# Revit family: boiler_eutectic-cast-iron_gt-530a_ea_ddr-americas_RVT2016
name_source: partatom
category: Equipement de génie climatique
revit_build: Autodesk Revit 2016 (Build: 20161004_0715(x64)
units: mm (PartAtom-declared; Revit-internal decimal feet)

## family parameters
Basée sur le plan de construction = Non
Cote de connecteur circulaire = Utiliser le diamètre
Couper avec des vides une fois chargée = Non
Numéro OmniClass = 23.75.10.11.14.11
Partagée = Non
Point de calcul de pièce = Non
Titre OmniClass = Cast-Iron Boilers
Toujours verticalement = Oui
Type d'élément = Normal

## types (18) — shared parameters
0 Message = User to Refer to De Dietrich Technical Data Sheet
04 CSI = 23 52 23
95 CSI = 15510
ASME Rating MAWP = 90
Approvals = CSA, MASS, NY-DEP, ASME, CSD-1, Low Nox certified, CRN
BMS Protocol = BACnet
Category = Mechanical Equipment
Code d'assemblage = D3020100
Description = Near-Condensing Eutectic Cast Iron Boiler
Efficiency = 88.00%
Fabricant = De Dietrich Boilers / DDR Americas Inc.
Firing Turndown Ratio = 5:1
Frequency = 60 Hz
Gas Pressure = 7-14 Inches w.c.
Gas-vent Category = I, II, III, IV, Sidewall vented and Direct vent (sealed combustion air)
Heat Exchanger Material = Cast Iron
Installation/Operating Instructions = http://www.dedietrichboilers.com
Low Nox - Optional = Oui
Manufacturer Fax = 519-650-1709
Max Water Temp Safety Limit = 248 °F
Nominal Width = 46 "
Phase = 1
Piping Layout = http://www.dedietrichboilers.com
Product Brochure = http://www.dedietrichboilers.com
Product Page URL = http://www.dedietrichboilers.com
SMARTBIM Object Version = 3
SMARTBIM URL = http://www.SMARTBIM.com
Specifications URL = http://www.dedietrichboilers.com
Subcategory = Gas-Oil Fired Eutectic Cast Iron Boiler
URL = http://www.dedietrichboilers.com
Voltage = 120 V
Water Operating Temp Range °F /°C = 104-212°F / 40-100°C
ØE = 5.5 "
zero-valued in all types: Gas Connection

## per-type parameters (varying)
- GT 530A-15: # Sections=15; #2 Fuel Oil Input=26 USGPH; A=98.18 "; B=34.14 "; Boiler-vent Connection=16 "; C=58.58 "; Dry Weight=7416.00 lb; Efficiency Natural Gas=85.00%; Full Load Amps=<15A; G=50 "; Gas Input=1099 kW; H=-1.22 "; Height=65.75 "; Installed Weight=8940.00 lb; K=0.75 "; L=88.39 "; M=7.4 "; Modèle=GT 530A-15; N=42.52 "; Nominal Height=65.75 "; Nominal Length=88.39 "; Output [Gas-Oil]=936.2 kW; P=32.09 "; Plates=Plastic Dark; R=7.87 "; Radius F=8 "; Unit=Paint Ivory Glossy; Water Capacity=183.1 gal; Water Resistance Delta T -18 F (Ft. H2O)=3.277; Water Resistance Delta T -27 F (Ft. H2O)=1.456; Water Resistance Delta T -36 F (Ft. H2O)=0.819; _C=58.58 "; _K=0.75 "; ØF=7.88 "
- GT 530A-16: # Sections=16; #2 Fuel Oil Input=27.5 USGPH; A=102.56 "; B=34.14 "; Boiler-vent Connection=16 "; C=58.58 "; Dry Weight=7851.00 lb; Efficiency Natural Gas=0.00%; Full Load Amps=<15A; G=5.9 "; Gas Input=1162 kW; H=-1.18 "; Height=65.75 "; Installed Weight=9460.00 lb; K=0.71 "; L=92.72 "; M=7.44 "; Modèle=GT 530A-16; N=42.52 "; Nominal Height=65.75 "; Nominal Length=92.72 "; Output [Gas-Oil]=990.2 kW; P=32.09 "; Plates=Aluminum Anodized; R=7.87 "; Radius F=8 "; Unit=Aluminum Polished; Water Capacity=193.2 gal; Water Resistance Delta T -18 F (Ft. H2O)=1.085; Water Resistance Delta T -27 F (Ft. H2O)=0.483; Water Resistance Delta T -36 F (Ft. H2O)=0.271; _C=58.58 "; _K=0.71 "; ØF=7.88 "
- GT 530A-17: # Sections=17; #2 Fuel Oil Input=29.5 USGPH; A=106.93 "; B=34.14 "; Boiler-vent Connection=16 "; C=58.58 "; Dry Weight=8280.00 lb; Efficiency Natural Gas=85.00%; Full Load Amps=<15A; G=14.57 "; Gas Input=1247 kW; H=-0.35 "; Height=65.75 "; Installed Weight=9970.00 lb; K=0.12 "; L=96.26 "; M=8.26 "; Modèle=GT 530A-17; N=42.52 "; Nominal Height=65.75 "; Nominal Length=96.26 "; Output [Gas-Oil]=1062.2 kW; P=32.09 "; Plates=Aluminum Anodized; R=7.87 "; Radius F=8 "; Unit=Aluminum Polished; Water Capacity=203.2 gal; Water Resistance Delta T -18 F (Ft. H2O)=1.279; Water Resistance Delta T -27 F (Ft. H2O)=0.569; Water Resistance Delta T -36 F (Ft. H2O)=0.32; _C=58.58 "; _K=0.12 "; ØF=7.88 "
- GT 530A-18: # Sections=18; #2 Fuel Oil Input=31 USGPH; A=112.68 "; B=34.14 "; Boiler-vent Connection=16 "; C=59.2 "; Dry Weight=8719.00 lb; Efficiency Natural Gas=0.00%; Full Load Amps=<15A; G=14.57 "; Gas Input=1310 kW; H=-0.32 "; Height=65.75 "; Installed Weight=10495.00 lb; K=0.16 "; L=100.59 "; M=9.29 "; Modèle=GT 530A-18; N=45.52 "; Nominal Height=65.75 "; Nominal Length=100.59 "; Output [Gas-Oil]=1188.3 kW; P=32.09 "; Plates=Aluminum Anodized; R=7.87 "; Radius F=8 "; Unit=Aluminum Polished; Water Capacity=213.2 gal; Water Resistance Delta T -18 F (Ft. H2O)=1.446; Water Resistance Delta T -27 F (Ft. H2O)=0.643; Water Resistance Delta T -36 F (Ft. H2O)=0.361; _C=59.2 "; _K=0.16 "; ØF=7.88 "
- GT 530A-19: # Sections=19; #2 Fuel Oil Input=33 USGPH; A=117.05 "; B=34.14 "; Boiler-vent Connection=16 "; C=59.2 "; Dry Weight=9092.00 lb; Efficiency Natural Gas=0.00%; Full Load Amps=<15A; G=14.57 "; Gas Input=1395 kW; H=0.51 "; Height=65.75 "; Installed Weight=10950.00 lb; K=0.98 "; L=104.13 "; M=10.12 "; Modèle=GT 530A-19; N=42.52 "; Nominal Height=65.75 "; Nominal Length=104.13 "; Output [Gas-Oil]=1188.3 kW; P=32.09 "; Plates=Aluminum Anodized; R=7.87 "; Radius F=8 "; Unit=Aluminum Polished; Water Capacity=223.3 gal; Water Resistance Delta T -18 F (Ft. H2O)=1.753; Water Resistance Delta T -27 F (Ft. H2O)=0.779; Water Resistance Delta T -36 F (Ft. H2O)=0.438; _C=59.2 "; _K=0.98 "; ØF=7.88 "
- GT 530A-20: # Sections=20; #2 Fuel Oil Input=34.5 USGPH; A=122.99 "; B=34.14 "; Boiler-vent Connection=16 "; C=59.2 "; Dry Weight=9575.00 lb; Efficiency Natural Gas=0.00%; Full Load Amps=<15A; G=25.59 "; Gas Input=1458 kW; H=-1.42 "; Height=65.75 "; Installed Weight=11565.00 lb; K=0.95 "; L=112.01 "; M=8.19 "; Modèle=GT 530A-20; N=42.52 "; Nominal Height=65.75 "; Nominal Length=112.01 "; Output [Gas-Oil]=1242.3 kW; P=32.09 "; Plates=Aluminum Anodized; R=7.87 "; Radius F=8 "; Unit=Aluminum Polished; Water Capacity=239.1 gal; Water Resistance Delta T -18 F (Ft. H2O)=1.999; Water Resistance Delta T -27 F (Ft. H2O)=0.889; Water Resistance Delta T -36 F (Ft. H2O)=0.5; _C=59.2 "; _K=0.95 "; ØF=7.88 "
- GT 530A-21: # Sections=21; #2 Fuel Oil Input=36 USGPH; A=127.36 "; B=34.14 "; Boiler-vent Connection=16 "; C=59.2 "; Dry Weight=10004.00 lb; Efficiency Natural Gas=0.00%; Full Load Amps=<15A; G=25.59 "; Gas Input=1521 kW; H=-1.38 "; Height=65.75 "; Installed Weight=12080.00 lb; K=0.91 "; L=116.34 "; M=8.22 "; Modèle=GT 530A-21; N=45.52 "; Nominal Height=65.75 "; Nominal Length=116.34 "; Output [Gas-Oil]=1296.3 kW; P=32.09 "; Plates=Aluminum Anodized; R=7.87 "; Radius F=9 "; Unit=Aluminum Polished; Water Capacity=249.1 gal; Water Resistance Delta T -18 F (Ft. H2O)=2.209; Water Resistance Delta T -27 F (Ft. H2O)=0.982; Water Resistance Delta T -36 F (Ft. H2O)=0.552; _C=59.2 "; _K=0.91 "; ØF=9 "
- GT 530A-22: # Sections=22; #2 Fuel Oil Input=38 USGPH; A=131.73 "; B=34.14 "; Boiler-vent Connection=18 "; C=59.2 "; Dry Weight=10437.00 lb; Efficiency Natural Gas=0.00%; Full Load Amps=<15A; G=25.59 "; Gas Input=1606 kW; H=-0.55 "; Height=65.75 "; Installed Weight=12595.00 lb; K=0.08 "; L=119.88 "; M=9.05 "; Modèle=GT 530A-22; N=42.52 "; Nominal Height=65.75 "; Nominal Length=119.88 "; Output [Gas-Oil]=1368.3 kW; P=32.09 "; Plates=Aluminum Anodized; R=7.87 "; Radius F=9 "; Unit=Aluminum Polished; Water Capacity=259.2 gal; Water Resistance Delta T -18 F (Ft. H2O)=2.476; Water Resistance Delta T -27 F (Ft. H2O)=1.101; Water Resistance Delta T -36 F (Ft. H2O)=0.619; _C=59.2 "; _K=0.08 "; ØF=9 "
- GT 530A-23: # Sections=23; #2 Fuel Oil Input=39.5 USGPH; A=131.73 "; B=34.14 "; Boiler-vent Connection=18 "; C=59.2 "; Dry Weight=10869.00 lb; Efficiency Natural Gas=0.00%; Full Load Amps=<15A; G=38.58 "; Gas Input=1669 kW; H=-0.51 "; Height=65.75 "; Installed Weight=13110.00 lb; K=0.04 "; L=124.21 "; M=9.05 "; Modèle=GT 530A-23; N=42.52 "; Nominal Height=65.75 "; Nominal Length=124.21 "; Output [Gas-Oil]=1422.3 kW; P=32.09 "; Plates=Aluminum Anodized; R=7.87 "; Radius F=9 "; Unit=Aluminum Polished; Water Capacity=269.2 gal; Water Resistance Delta T -18 F (Ft. H2O)=2.703; Water Resistance Delta T -27 F (Ft. H2O)=1.201; Water Resistance Delta T -36 F (Ft. H2O)=0.676; _C=59.2 "; _K=0.04 "; ØF=9 "
- GT 530A-24: # Sections=24; #2 Fuel Oil Input=41.5 USGPH; A=140.47 "; B=34.14 "; Boiler-vent Connection=18 "; C=59.2 "; Dry Weight=11259.00 lb; Efficiency Natural Gas=0.00%; Full Load Amps=<15A; G=38.58 "; Gas Input=1754 kW; H=0.32 "; Height=65.75 "; Installed Weight=13585.00 lb; K=0.79 "; L=127.76 "; M=9.92 "; Modèle=GT 530A-24; N=42.52 "; Nominal Height=65.75 "; Nominal Length=127.76 "; Output [Gas-Oil]=1494.3 kW; P=32.09 "; Plates=Aluminum Anodized; R=7.87 "; Radius F=9 "; Unit=Aluminum Polished; Water Capacity=279.3 gal; Water Resistance Delta T -18 F (Ft. H2O)=3.014; Water Resistance Delta T -27 F (Ft. H2O)=1.339; Water Resistance Delta T -36 F (Ft. H2O)=0.753; _C=59.2 "; _K=0.79 "; ØF=9 "
- GT 530A-25: # Sections=25; #2 Fuel Oil Input=43 USGPH; A=144.84 "; B=34.14 "; Boiler-vent Connection=18 "; C=59.2 "; Dry Weight=11678.00 lb; Efficiency Natural Gas=0.00%; Full Load Amps=<15A; G=38.58 "; Gas Input=1817 kW; H=0.35 "; Height=65.75 "; Installed Weight=14085.00 lb; K=0.83 "; L=132.09 "; M=9.96 "; Modèle=GT 530A-25; N=42.52 "; Nominal Height=65.75 "; Nominal Length=132.09 "; Output [Gas-Oil]=1548.3 kW; P=32.09 "; Plates=Aluminum Anodized; R=7.87 "; Radius F=9 "; Unit=Aluminum Polished; Water Capacity=289.4 gal; Water Resistance Delta T -18 F (Ft. H2O)=3.269; Water Resistance Delta T -27 F (Ft. H2O)=1.452; Water Resistance Delta T -36 F (Ft. H2O)=0.817; _C=59.2 "; _K=0.83 "; ØF=9 "
- GT 530AE-26: # Sections=26; #2 Fuel Oil Input=43.8 USGPH; A=154.37 "; B=37.14 "; Boiler-vent Connection=20 "; C=65 "; Dry Weight=12111.00 lb; Efficiency Natural Gas=0.00%; Full Load Amps=<15A fused; G=41.6 "; Gas Input=1900 kW; H=1.02 "; Height=68.75 "; Installed Weight=0.00 lb; K=1.81 "; L=138.8 "; M=19.53 "; Modèle=GT 530A-26; N=45.52 "; Nominal Height=68.75 "; Nominal Length=138.8 "; Output [Gas-Oil]=1618.8 kW; P=35.09 "; Plates=Aluminum Anodized; R=10.87 "; Radius F=10 "; Unit=Aluminum Polished; Water Capacity=299.4 gal; Water Resistance Delta T -18 F (Ft. H2O)=3.48; Water Resistance Delta T -27 F (Ft. H2O)=1.55; Water Resistance Delta T -36 F (Ft. H2O)=0.87; _C=65 "; _K=1.81 "; ØF=10 "
- GT 530AE-29: # Sections=29; #2 Fuel Oil Input=49.7 USGPH; A=167.48 "; B=37.14 "; Boiler-vent Connection=20 "; C=65 "; Dry Weight=13281.00 lb; Efficiency Natural Gas=85.00%; Full Load Amps=<15A  fused; G=41.6 "; Gas Input=2100 kW; H=-1.61 "; Height=68.75 "; Installed Weight=0.00 lb; K=0.82 "; L=150.2 "; M=16.88 "; Modèle=GT 530A-29; N=45.52 "; Nominal Height=68.75 "; Nominal Length=150.2 "; Output [Gas-Oil]=1789.4 kW; P=35.09 "; Plates=Aluminum Anodized; R=10.87 "; Radius F=10 "; Unit=Aluminum Polished; Water Capacity=329.7 gal; Water Resistance Delta T -18 F (Ft. H2O)=4.26; Water Resistance Delta T -27 F (Ft. H2O)=1.9; Water Resistance Delta T -36 F (Ft. H2O)=1.06; _C=65 "; _K=0.82 "; ØF=10 "
- GT 530AE-27: # Sections=27; #2 Fuel Oil Input=45.8 USGPH; A=158.74 "; B=37.14 "; Boiler-vent Connection=20 "; C=65 "; Dry Weight=12501.00 lb; Efficiency Natural Gas=0.00%; Full Load Amps=<15A fused; G=41.6 "; Gas Input=1950 kW; H=-2.48 "; Height=68.75 "; Installed Weight=0.00 lb; K=1.69 "; L=142.3 "; M=19.56 "; Modèle=GT 530A-27; N=45.52 "; Nominal Height=68.75 "; Nominal Length=142.3 "; Output [Gas-Oil]=1661.1 kW; P=35.09 "; Plates=Aluminum Anodized; R=10.87 "; Radius F=10 "; Unit=Aluminum Polished; Water Capacity=309.5 gal; Water Resistance Delta T -18 F (Ft. H2O)=3.67; Water Resistance Delta T -27 F (Ft. H2O)=1.63; Water Resistance Delta T -36 F (Ft. H2O)=0.92; _C=65 "; _K=1.69 "; ØF=10 "
- GT 530AE-28: # Sections=28; #2 Fuel Oil Input=47.7 USGPH; A=163.11 "; B=37.14 "; Boiler-vent Connection=20 "; C=65 "; Dry Weight=12501.00 lb; Efficiency Natural Gas=0.00%; Full Load Amps=<15A fused; G=41.6 "; Gas Input=2000 kW; H=-2.44 "; Height=68.75 "; Installed Weight=0.00 lb; K=1.65 "; L=146.6 "; M=16.06 "; Modèle=GT 530A-28; N=45.52 "; Nominal Height=68.75 "; Nominal Length=146.6 "; Output [Gas-Oil]=1704.2 kW; P=35.09 "; Plates=Aluminum Anodized; R=10.87 "; Radius F=10 "; Unit=Aluminum Polished; Water Capacity=319.6 gal; Water Resistance Delta T -18 F (Ft. H2O)=3.86; Water Resistance Delta T -27 F (Ft. H2O)=1.72; Water Resistance Delta T -36 F (Ft. H2O)=0.97; _C=65 "; _K=1.65 "; ØF=10 "
- GT 530AE-30: # Sections=30; #2 Fuel Oil Input=51.6 USGPH; A=171.85 "; B=37.14 "; Boiler-vent Connection=20 "; C=65 "; Dry Weight=13671.00 lb; Efficiency Natural Gas=85.00%; Full Load Amps=<15A  fused; G=41.6 "; Gas Input=2200 kW; H=-5.11 "; Height=68.75 "; Installed Weight=0.00 lb; K=4.33 "; L=154.05 "; M=16.93 "; Modèle=GT 530A-30; N=45.52 "; Nominal Height=68.75 "; Nominal Length=154.05 "; Output [Gas-Oil]=1874.1 kW; P=35.09 "; Plates=Aluminum Anodized; R=10.87 "; Radius F=10 "; Unit=Aluminum Polished; Water Capacity=339.8 gal; Water Resistance Delta T -18 F (Ft. H2O)=4.67; Water Resistance Delta T -27 F (Ft. H2O)=2.07; Water Resistance Delta T -36 F (Ft. H2O)=1.17; _C=65 "; _K=4.33 "; ØF=10 "
- GT 530AE-31: # Sections=31; #2 Fuel Oil Input=53.6 USGPH; A=176.22 "; B=37.14 "; Boiler-vent Connection=20 "; C=65 "; Dry Weight=14061.00 lb; Efficiency Natural Gas=85.00%; Full Load Amps=<15A  fused; G=41.6 "; Gas Input=2300 kW; H=-5.07 "; Height=68.75 "; Installed Weight=0.00 lb; K=4.29 "; L=158 "; M=17.71 "; Modèle=GT 530A-31; N=45.52 "; Nominal Height=68.75 "; Nominal Length=158 "; Output [Gas-Oil]=1959.9 kW; P=35.09 "; Plates=Aluminum Anodized; R=10.87 "; Radius F=10 "; Unit=Aluminum Polished; Water Capacity=349.9 gal; Water Resistance Delta T -18 F (Ft. H2O)=5.1; Water Resistance Delta T -27 F (Ft. H2O)=2.27; Water Resistance Delta T -36 F (Ft. H2O)=1.28; _C=65 "; _K=4.29 "; ØF=10 "
- GT 530AE-32: # Sections=32; #2 Fuel Oil Input=55.5 USGPH; A=196.65 "; B=37.14 "; Boiler-vent Connection=20 "; C=65 "; Dry Weight=14451.00 lb; Efficiency Natural Gas=85.00%; Full Load Amps=<15A  fused; G=41.6 "; Gas Input=2400kW; H=-4.25 "; Height=68.75 "; Installed Weight=0.00 lb; K=3.46 "; L=162.4 "; M=17.79 "; Modèle=GT 530A-32; N=45.52 "; Nominal Height=68.75 "; Nominal Length=162.4 "; Output [Gas-Oil]=2045.1 kW; P=35.09 "; Plates=Aluminum Anodized; R=10.87 "; Radius F=10 "; Unit=Aluminum Polished; Water Capacity=360.0 gal; Water Resistance Delta T -18 F (Ft. H2O)=5.56; Water Resistance Delta T -27 F (Ft. H2O)=2.5; Water Resistance Delta T -36 F (Ft. H2O)=1.39; _C=65 "; _K=3.46 "; ØF=10 "

## geometry (parser evidence)
native form markers: Blend x16, Sweep x5
no freeform markers — native parametric forms only
